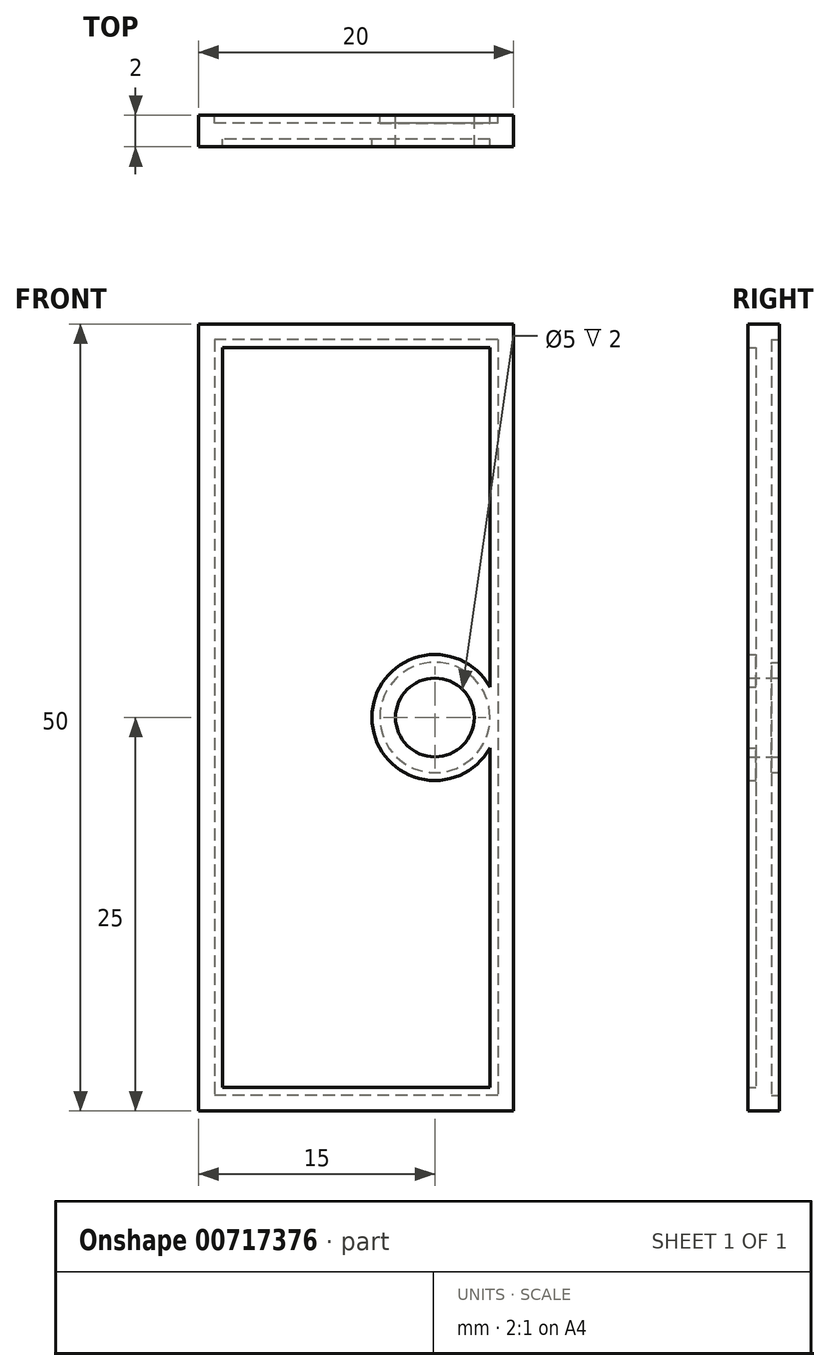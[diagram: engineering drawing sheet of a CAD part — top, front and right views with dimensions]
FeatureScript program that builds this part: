
annotation { "Feature Type Name" : "Feature", "Feature Type Description" : "" }
export const myFeature = defineFeature(function(context is Context, id is Id, definition is map)
    precondition{}
    {
        {
            var Q0;
            Q0=qCreatedBy(makeId("Front.planeOp"),FACE);
            var sketch = newSketch(context, id + "F0", { "sketchPlane" : qUnion([Q0])});
            skLineSegment(sketch, "E0.bottom", {"start": v(10, 25) * mm, "end": v(-10, 25) * mm});
            skLineSegment(sketch, "E0.top", {"start": v(10, -25) * mm, "end": v(-10, -25) * mm});
            skLineSegment(sketch, "E0.left", {"start": v(10, 25) * mm, "end": v(10, -25) * mm});
            skLineSegment(sketch, "E0.right", {"start": v(-10, 25) * mm, "end": v(-10, -25) * mm});
            skPoint(sketch, "E0.middle", {"position": v(0, 0) * mm});
            skCircle(sketch, "E1", {"center": v(5, 0) * mm, "radius": 2.5 * mm});
            skPoint(sketch, "E1.centerSnap0", {"position": v(10, 0) * mm});
            skSolve(sketch);
        }
        {
            var Q0;
            Q0=makeQuery(id+"F0.imprint","IMPRINT",FACE,{"disambiguationData":[TD([[makeQuery(id+"F0.imprint","IMPRINT",EDGE,{"derivedFrom":sQuery(id+"F0.wireOp",EDGE,"E0.bottom")}),1.0]])]});
            extrude(context, id + "F1", {"entities" : qUnion([Q0]), "endBound" : BoundingType.SYMMETRIC, "depth" : 2 * mm, "offsetDistance" : 25 * mm});
        }
        {
            var Q0;
            Q0=makeQuery(id+"F1.opExtrude","CAP_FACE",FACE,{"disambiguationData":[OSD([sQuery(id+"F0.wireOp",EDGE,"E0.bottom"),sQuery(id+"F0.wireOp",EDGE,"E0.top"),sQuery(id+"F0.wireOp",EDGE,"E0.left"),sQuery(id+"F0.wireOp",EDGE,"E0.right"),sQuery(id+"F0.wireOp",EDGE,"E1")])],"isStart":false});
            shell(context, id + "F2", {"entities" : qUnion([Q0]), "thickness" : 1.5 * mm});
        }
        {
            var Q0;
            Q0=makeQuery(id+"F1.opExtrude","CAP_FACE",FACE,{"disambiguationData":[OSD([sQuery(id+"F0.wireOp",EDGE,"E0.bottom"),sQuery(id+"F0.wireOp",EDGE,"E0.top"),sQuery(id+"F0.wireOp",EDGE,"E0.left"),sQuery(id+"F0.wireOp",EDGE,"E0.right"),sQuery(id+"F0.wireOp",EDGE,"E1")])],"isStart":true});
            shell(context, id + "F3", {"entities" : qUnion([Q0]), "thickness" : 1 * mm});
        }
    });
